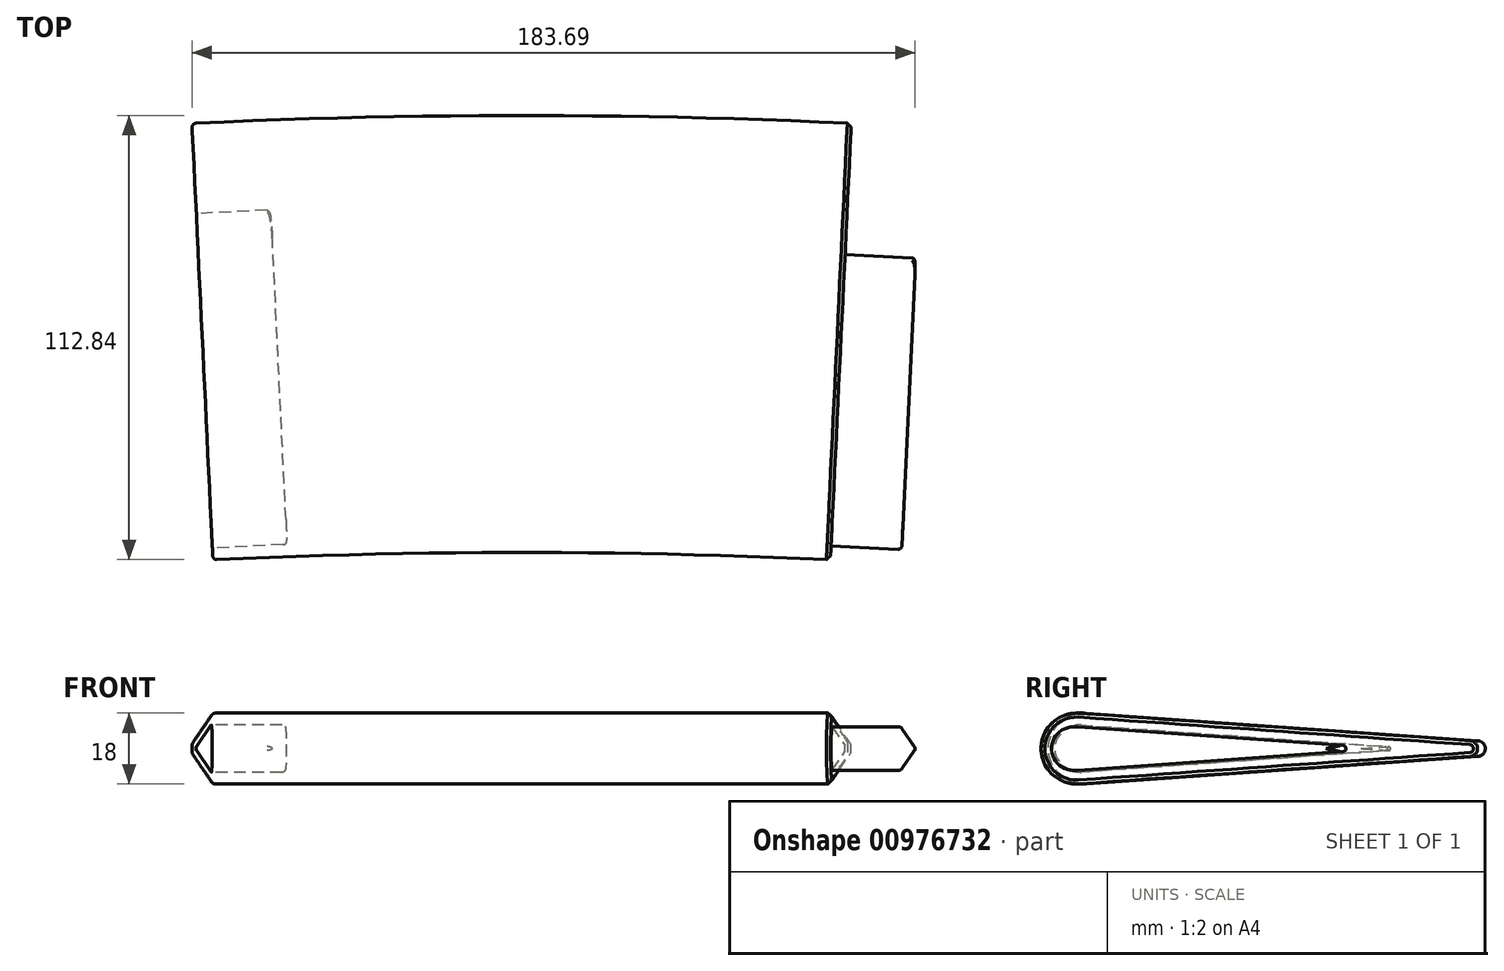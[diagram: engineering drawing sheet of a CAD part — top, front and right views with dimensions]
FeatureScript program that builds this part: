
annotation { "Feature Type Name" : "Feature", "Feature Type Description" : "" }
export const myFeature = defineFeature(function(context is Context, id is Id, definition is map)
    precondition{}
    {
        {
            var Q0;
            Q0=qCreatedBy(makeId("Right.planeOp"),FACE);
            var sketch = newSketch(context, id + "F0", { "sketchPlane" : qUnion([Q0])});
            skArc(sketch, "E0", {"start": v(-49.37, 8.98) * mm, "mid": v(-59, 0) * mm, "end": v(-49.37, -8.98) * mm});
            skArc(sketch, "E1", {"start": v(50.14, -2) * mm, "mid": v(52, 0) * mm, "end": v(50.14, 2) * mm});
            skLineSegment(sketch, "E2", {"start": v(-49.37, 8.98) * mm, "end": v(50.14, 2) * mm});
            skLineSegment(sketch, "E3", {"start": v(-49.37, -8.98) * mm, "end": v(50.14, -2) * mm});
            skLineSegment(sketch, "E4", {"start": v(-64.73, 0) * mm, "end": v(60.4, 0) * mm, "construction": true});
            skLineSegment(sketch, "E5", {"start": v(50.3, 9.61) * mm, "end": v(50.3, -14.26) * mm, "construction": true});
            skLineSegment(sketch, "E6", {"start": v(-49.74, 17.63) * mm, "end": v(-49.74, -19.67) * mm, "construction": true});
            skSolve(sketch);
        }
        {
            var Q0;
            Q0=qCreatedBy(makeId("Right.planeOp"),FACE);
            var sketch = newSketch(context, id + "F1", { "sketchPlane" : qUnion([Q0])});
            skLineSegment(sketch, "E7", {"start": v(-1693.74, 0) * mm, "end": v(-1693.74, 97.3) * mm, "construction": true});
            skSolve(sketch);
        }
        {
            var Q0;
            Q0=makeQuery(id+"F0.imprint","IMPRINT",FACE,{"disambiguationData":[TD([[makeQuery(id+"F0.imprint","IMPRINT",EDGE,{"derivedFrom":sQuery(id+"F0.wireOp",EDGE,"E0")}),1.0]])]});
            var Q1;
            Q1=sQuery(id+"F1.wireOp",EDGE,"E7");
            revolve(context, id + "F2", {"surfaceOperationType" : NewSurfaceOperationType.NEW, "entities" : qUnion([Q0]), "axis" : qUnion([Q1]), "revolveType" : RevolveType.SYMMETRIC, "angle" : 5.5 * degree});
        }
        {
            var Q0;
            Q0=makeQuery(id+"F2.opRevolve","CAP_FACE",FACE,{"disambiguationData":[OSD([sQuery(id+"F0.wireOp",EDGE,"E0"),sQuery(id+"F0.wireOp",EDGE,"E1"),sQuery(id+"F0.wireOp",EDGE,"E2"),sQuery(id+"F0.wireOp",EDGE,"E3")])],"isStart":true});
            var sketch = newSketch(context, id + "F3", { "sketchPlane" : qUnion([Q0])});
            skArc(sketch, "E8.0", {"start": v(-47.66, 5.49) * mm, "mid": v(-53.55, 0) * mm, "end": v(-47.66, -5.49) * mm});
            skLineSegment(sketch, "E9.0", {"start": v(-47.66, 5.49) * mm, "end": v(19.86, 0.75) * mm});
            skLineSegment(sketch, "E10.0", {"start": v(-47.66, -5.49) * mm, "end": v(19.86, -0.75) * mm});
            skArc(sketch, "E11.filletArc", {"start": v(19.86, -0.75) * mm, "mid": v(20.56, 0) * mm, "end": v(19.86, 0.75) * mm});
            skSolve(sketch);
        }
        {
            var Q0;
            Q0=makeQuery(id+"F2.opRevolve","CAP_EDGE",EDGE,{"disambiguationData":[OSD([sQuery(id+"F0.wireOp",EDGE,"E2")])],"isStart":true});
            chamfer(context, id + "F4", {"entities" : qUnion([Q0]), "width" : 1 * mm, "tangentPropagation" : true});
        }
        {
            var Q0;
            Q0=makeQuery(id+"F2.opRevolve","CAP_FACE",FACE,{"disambiguationData":[OSD([sQuery(id+"F0.wireOp",EDGE,"E0"),sQuery(id+"F0.wireOp",EDGE,"E1"),sQuery(id+"F0.wireOp",EDGE,"E2"),sQuery(id+"F0.wireOp",EDGE,"E3")])],"isStart":false});
            var sketch = newSketch(context, id + "F5", { "sketchPlane" : qUnion([Q0])});
            skLineSegment(sketch, "E12.0", {"start": v(47.63, 5.99) * mm, "end": v(-30.56, 0.5) * mm});
            skArc(sketch, "E13.0", {"start": v(47.63, 5.99) * mm, "mid": v(54.05, 0) * mm, "end": v(47.63, -5.99) * mm});
            skLineSegment(sketch, "E14.0", {"start": v(47.63, -5.99) * mm, "end": v(-30.56, -0.5) * mm});
            skArc(sketch, "E15.filletArc", {"start": v(-30.56, 0.5) * mm, "mid": v(-31.02, 0) * mm, "end": v(-30.56, -0.5) * mm});
            skSolve(sketch);
        }
        {
            var Q0;
            Q0 = qSketchRegion(id + "F5", true);
            extrude(context, id + "F6", {"entities" : qUnion([Q0]), "operationType" : NewBodyOperationType.REMOVE, "oppositeDirection" : true, "depth" : 19 * mm, "offsetDistance" : 25 * mm});
        }
        {
            var Q0;
            Q0=makeQuery(id+"F2.opRevolve","CAP_EDGE",EDGE,{"disambiguationData":[OSD([sQuery(id+"F0.wireOp",EDGE,"E2")])],"isStart":false});
            var Q1;
            Q1=makeQuery(id+"F6.boolean.opBoolean","COPY",EDGE,{"derivedFrom":makeQuery(id+"F6.opExtrude","CAP_EDGE",EDGE,{"disambiguationData":[OSD([sQuery(id+"F5.wireOp",EDGE,"E12.0")])],"isStart":true})});
            var Q2;
            Q2=makeQuery(id+"F6.boolean.opBoolean","COPY",EDGE,{"derivedFrom":makeQuery(id+"F6.opExtrude","CAP_EDGE",EDGE,{"disambiguationData":[OSD([sQuery(id+"F5.wireOp",EDGE,"E14.0")])],"isStart":false})});
            fillet(context, id + "F7", {"entities" : qUnion([Q0, Q1, Q2]), "radius" : 1 * mm, "tangentPropagation" : true, "allowEdgeOverflow" : false});
        }
        {
            var Q0;
            Q0=makeQuery(id+"F3.imprint","IMPRINT",FACE,{"disambiguationData":[TD([[makeQuery(id+"F3.imprint","IMPRINT",EDGE,{"derivedFrom":sQuery(id+"F3.wireOp",EDGE,"E8.0")}),1.0]])]});
            extrude(context, id + "F8", {"entities" : qUnion([Q0]), "operationType" : NewBodyOperationType.ADD, "depth" : 15 * mm, "offsetDistance" : 25 * mm});
        }
        {
            var Q0;
            Q0=makeQuery(id+"F8.opExtrude","CAP_EDGE",EDGE,{"disambiguationData":[OSD([sQuery(id+"F3.wireOp",EDGE,"E9.0")])],"isStart":true});
            var Q1;
            Q1=makeQuery(id+"F8.opExtrude","CAP_EDGE",EDGE,{"disambiguationData":[OSD([sQuery(id+"F3.wireOp",EDGE,"E9.0")])],"isStart":false});
            fillet(context, id + "F9", {"entities" : qUnion([Q0, Q1]), "radius" : 1 * mm, "tangentPropagation" : true, "allowEdgeOverflow" : false});
        }
        {
            var Q0;
            Q0=makeQuery(id+"F3.imprint","IMPRINT",FACE,{"disambiguationData":[TD([[makeQuery(id+"F3.imprint","IMPRINT",EDGE,{"derivedFrom":sQuery(id+"F3.wireOp",EDGE,"E8.0")}),1.0]])]});
            extrude(context, id + "F10", {"entities" : qUnion([Q0]), "operationType" : NewBodyOperationType.ADD, "depth" : 18 * mm, "offsetDistance" : 25 * mm});
        }
        {
            var Q0;
            Q0=makeQuery(id+"F10.opExtrude","CAP_EDGE",EDGE,{"disambiguationData":[OSD([sQuery(id+"F3.wireOp",EDGE,"E9.0")])],"isStart":false});
            fillet(context, id + "F11", {"entities" : qUnion([Q0]), "radius" : 1 * mm, "tangentPropagation" : true, "allowEdgeOverflow" : false});
        }
    });
